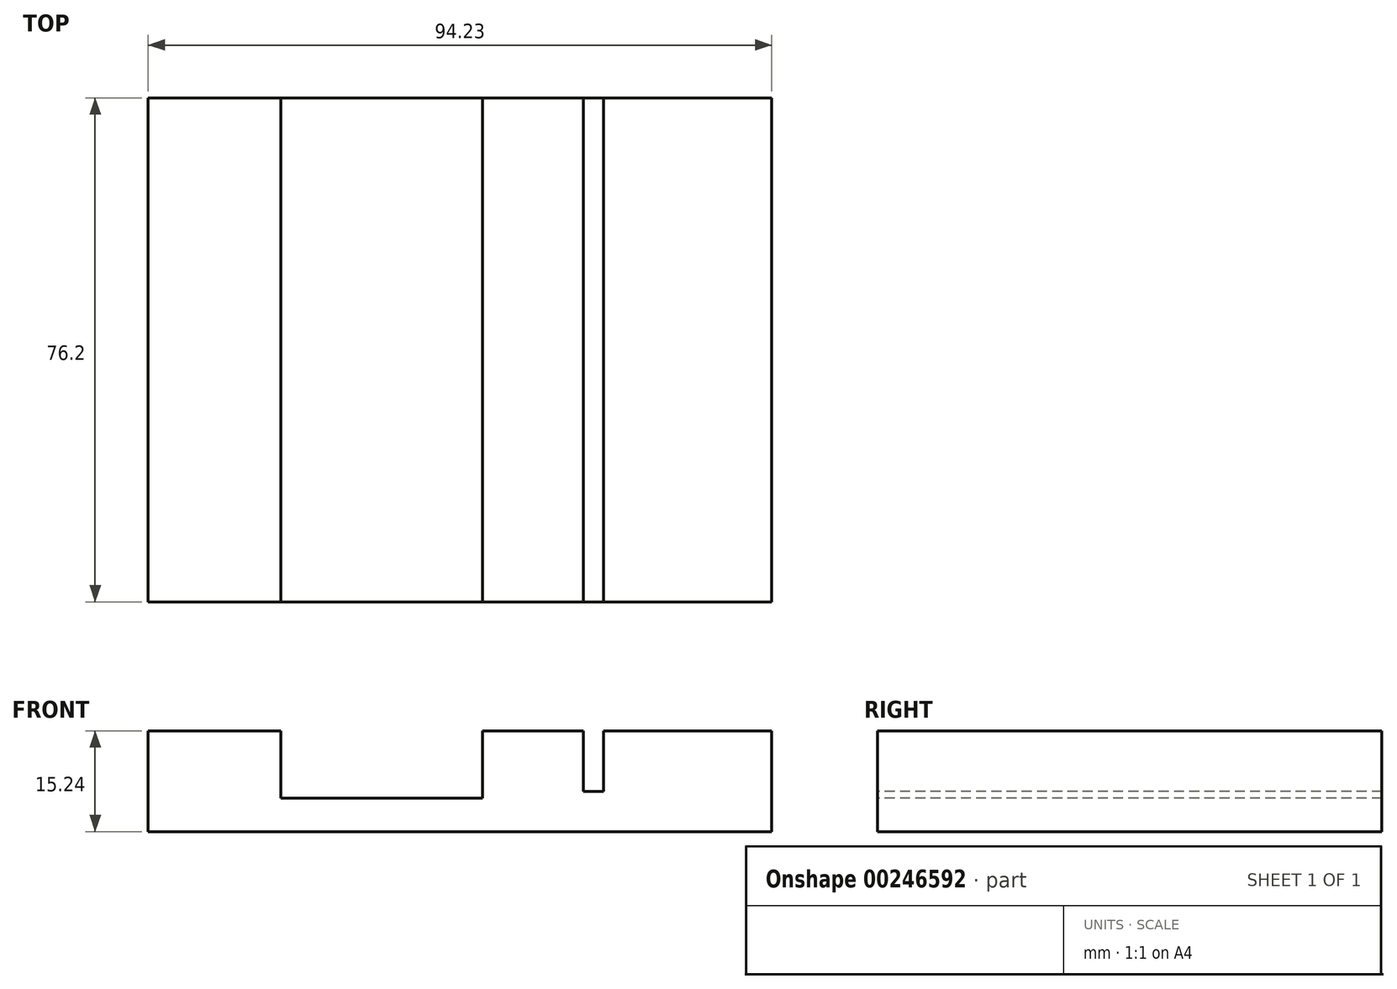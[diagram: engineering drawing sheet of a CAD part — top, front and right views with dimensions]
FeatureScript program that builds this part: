
annotation { "Feature Type Name" : "Feature", "Feature Type Description" : "" }
export const myFeature = defineFeature(function(context is Context, id is Id, definition is map)
    precondition{}
    {
        {
            var Q0;
            Q0=qCreatedBy(makeId("Top.planeOp"),FACE);
            var sketch = newSketch(context, id + "F0", { "sketchPlane" : qUnion([Q0])});
            skLineSegment(sketch, "E0.bottom", {"start": v(0, 0) * mm, "end": v(101.6, 0) * mm});
            skLineSegment(sketch, "E0.top", {"start": v(0, 76.2) * mm, "end": v(101.6, 76.2) * mm});
            skLineSegment(sketch, "E0.left", {"start": v(0, 0) * mm, "end": v(0, 76.2) * mm});
            skLineSegment(sketch, "E0.right", {"start": v(101.6, 0) * mm, "end": v(101.6, 76.2) * mm});
            skSolve(sketch);
        }
        {
            var Q0;
            Q0=makeQuery(id+"F0.imprint","IMPRINT",FACE,{"disambiguationData":[TD([[makeQuery(id+"F0.imprint","IMPRINT",EDGE,{"derivedFrom":sQuery(id+"F0.wireOp",EDGE,"E0.bottom")}),1.0]])]});
            extrude(context, id + "F1", {"entities" : qUnion([Q0]), "depth" : 15.24 * mm});
        }
        {
            var Q0;
            Q0=makeQuery(id+"F1.opExtrude","CAP_FACE",FACE,{"disambiguationData":[OSD([sQuery(id+"F0.wireOp",EDGE,"E0.bottom"),sQuery(id+"F0.wireOp",EDGE,"E0.top"),sQuery(id+"F0.wireOp",EDGE,"E0.left"),sQuery(id+"F0.wireOp",EDGE,"E0.right")])],"isStart":false});
            var sketch = newSketch(context, id + "F2", { "sketchPlane" : qUnion([Q0])});
            skLineSegment(sketch, "E1.bottom", {"start": v(101.6, 76.2) * mm, "end": v(76.2, 76.2) * mm});
            skLineSegment(sketch, "E1.top", {"start": v(101.6, 0) * mm, "end": v(76.2, 0) * mm});
            skLineSegment(sketch, "E1.left", {"start": v(101.6, 76.2) * mm, "end": v(101.6, 0) * mm});
            skLineSegment(sketch, "E1.right", {"start": v(76.2, 76.2) * mm, "end": v(76.2, 0) * mm});
            skLineSegment(sketch, "E2.bottom", {"start": v(76.2, 76.2) * mm, "end": v(73.15, 76.2) * mm});
            skLineSegment(sketch, "E2.top", {"start": v(76.2, 0) * mm, "end": v(73.15, 0) * mm});
            skLineSegment(sketch, "E2.right", {"start": v(73.15, 76.2) * mm, "end": v(73.15, 0) * mm});
            skSolve(sketch);
        }
        {
            var Q0;
            Q0=makeQuery(id+"F2.imprint","IMPRINT",FACE,{"disambiguationData":[TD([[makeQuery(id+"F2.imprint","IMPRINT",EDGE,{"derivedFrom":sQuery(id+"F2.wireOp",EDGE,"E2.bottom")}),-1.0]])]});
            extrude(context, id + "F3", {"entities" : qUnion([Q0]), "operationType" : NewBodyOperationType.REMOVE, "oppositeDirection" : true, "depth" : 9.14 * mm});
        }
        {
            var Q0;
            {var subQ0=sQuery(id+"F0.wireOp",EDGE,"E0.bottom");var subQ1=sQuery(id+"F0.wireOp",EDGE,"E0.top");var subQ2=sQuery(id+"F0.wireOp",EDGE,"E0.left");Q0=makeQuery(id+"F3.boolean.opBoolean","SPLIT",FACE,{"disambiguationData":[TD([makeQuery(id+"F1.opExtrude","SWEPT_FACE",FACE,{"disambiguationData":[OSD([subQ2])]})])],"derivedFrom":makeQuery(id+"F1.opExtrude","CAP_FACE",FACE,{"disambiguationData":[OSD([subQ0,subQ1,subQ2,sQuery(id+"F0.wireOp",EDGE,"E0.right")])],"isStart":false})});}
            var sketch = newSketch(context, id + "F4", { "sketchPlane" : qUnion([Q0])});
            skLineSegment(sketch, "E3.bottom", {"start": v(73.15, 76.2) * mm, "end": v(57.91, 76.2) * mm});
            skLineSegment(sketch, "E3.top", {"start": v(73.15, 0) * mm, "end": v(57.91, 0) * mm});
            skLineSegment(sketch, "E3.left", {"start": v(73.15, 76.2) * mm, "end": v(73.15, 0) * mm});
            skLineSegment(sketch, "E3.right", {"start": v(57.91, 76.2) * mm, "end": v(57.91, 0) * mm});
            skLineSegment(sketch, "E4.bottom", {"start": v(57.91, 76.2) * mm, "end": v(27.43, 76.2) * mm});
            skLineSegment(sketch, "E4.top", {"start": v(57.91, 0) * mm, "end": v(27.43, 0) * mm});
            skLineSegment(sketch, "E4.right", {"start": v(27.43, 76.2) * mm, "end": v(27.43, 0) * mm});
            skSolve(sketch);
        }
        {
            var Q0;
            Q0=makeQuery(id+"F4.imprint","IMPRINT",FACE,{"disambiguationData":[TD([[makeQuery(id+"F4.imprint","IMPRINT",EDGE,{"derivedFrom":sQuery(id+"F4.wireOp",EDGE,"E4.bottom")}),-1.0]])]});
            extrude(context, id + "F5", {"entities" : qUnion([Q0]), "operationType" : NewBodyOperationType.REMOVE, "oppositeDirection" : true, "depth" : 10.16 * mm});
        }
        {
            var Q0;
            {var subQ0=sQuery(id+"F0.wireOp",EDGE,"E0.bottom");var subQ2=sQuery(id+"F0.wireOp",EDGE,"E0.top");var subQ4=sQuery(id+"F0.wireOp",EDGE,"E0.left");var subQ5=makeQuery(id+"F1.opExtrude","SWEPT_FACE",FACE,{"disambiguationData":[OSD([subQ4])]});Q0=makeQuery(id+"F5.boolean.opBoolean","SPLIT",FACE,{"disambiguationData":[TD([subQ5])],"derivedFrom":makeQuery(id+"F3.boolean.opBoolean","SPLIT",FACE,{"disambiguationData":[TD([subQ5])],"derivedFrom":makeQuery(id+"F1.opExtrude","CAP_FACE",FACE,{"disambiguationData":[OSD([subQ0,subQ2,subQ4,sQuery(id+"F0.wireOp",EDGE,"E0.right")])],"isStart":false})})});}
            var sketch = newSketch(context, id + "F6", { "sketchPlane" : qUnion([Q0])});
            skLineSegment(sketch, "E5.bottom", {"start": v(27.43, 76.2) * mm, "end": v(7.37, 76.2) * mm});
            skLineSegment(sketch, "E5.top", {"start": v(27.43, 0) * mm, "end": v(7.37, 0) * mm});
            skLineSegment(sketch, "E5.left", {"start": v(27.43, 76.2) * mm, "end": v(27.43, 0) * mm});
            skLineSegment(sketch, "E5.right", {"start": v(7.37, 76.2) * mm, "end": v(7.37, 0) * mm});
            skLineSegment(sketch, "E6.bottom", {"start": v(7.37, 76.2) * mm, "end": v(0, 76.2) * mm});
            skLineSegment(sketch, "E6.top", {"start": v(7.37, 0) * mm, "end": v(0, 0) * mm});
            skLineSegment(sketch, "E6.right", {"start": v(0, 76.2) * mm, "end": v(0, 0) * mm});
            skSolve(sketch);
        }
        {
            var Q0;
            Q0=makeQuery(id+"F6.imprint","IMPRINT",FACE,{"disambiguationData":[TD([[makeQuery(id+"F6.imprint","IMPRINT",EDGE,{"derivedFrom":sQuery(id+"F6.wireOp",EDGE,"E6.bottom")}),-1.0]])]});
            extrude(context, id + "F7", {"entities" : qUnion([Q0]), "operationType" : NewBodyOperationType.REMOVE, "oppositeDirection" : true, "depth" : 17.78 * mm});
        }
    });
